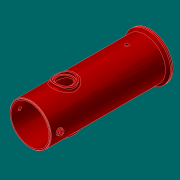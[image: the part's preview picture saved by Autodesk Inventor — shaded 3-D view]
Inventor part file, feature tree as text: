
AUTODESK INVENTOR PART (.ipt)
format: ipt  version: 2017.3 (Build 213256000, 256)  size: 425,472 bytes
history: native  units: in
note: dims shown in document units (in); Inventor stores cm internally (conversion verified against a paired STEP export)
features: extrude x11, sketch x8, fillet x4, chamfer x2, plane x2, pattern_circular x2, other x1
ambient origin geometry x8: Origin, YZ Plane, XZ Plane, XY Plane, X Axis, Y Axis, Z Axis, Center Point
bodies: Solid1 (feature_tree)
feature tree (30):
  extrude  "Extrusion1"  Depth=31.0in
  extrude  "Extrusion2"  Depth=34.75in
  extrude  "Extrusion3"  Depth=34.48in
  chamfer  "Chamfer1"  Distance=1.0in
  extrude  "Extrusion4"  Depth=0.125in TaperAngle=45.0deg
  chamfer  "Chamfer2"  Distance=0.5in
  fillet  "Fillet1"  Radius=0.0312in
  extrude  "Extrusion5"  Depth=17.3228in
  plane  "Work Plane1"
  sketch  "Sketch6"  dims[d16=0.0312in d17=0.125in d18=45.0deg d19=0.0312in]
  extrude  "Extrusion6"  Depth=0.0312in
  extrude  "Extrusion7"  Depth=0.0312in TaperAngle=0.0deg
  extrude  "Extrusion8"  Depth=0.0312in
  fillet  "Fillet2"  Radius=2.5in
  pattern_circular  "Circular Pattern1"  Count=212  [1 undecoded]
  plane  "Work Plane2"
  sketch  "Sketch7"  dims[d20=2.5984in d21=17.3228in]
  extrude  "Extrusion9"  Depth=0.0312in TaperAngle=0.0deg
  extrude  "Extrusion10"  Depth=0.0312in TaperAngle=0.0deg
  fillet  "Fillet3"  Radius=1.5in
  fillet  "Fillet4"  [1 undecoded]
  pattern_circular  "Circular Pattern2"  [2 undecoded]
  sketch  "Sketch1"  dims[d0=28.5in d1=31.0in]
  sketch  "Sketch2"  dims[d2=90.0in d3=0.0in d4=34.75in]
  sketch  "Sketch3"  dims[d5=2.0in d6=0.0in d7=34.48in d8=1.0in d9=0.0in]
  sketch  "Sketch4"  dims[d10=1.875in d11=0.125in d12=45.0deg]
  sketch  "Sketch5"  dims[d13=29.98in d14=0.5in d15=0.0in]
  sketch  "Sketch8"  dims[d22=10.5in d23=46.9291in d24=0.5in d25=0.0in d26=4.0in d27=2.5in d28=83.4646in d29=0.5in d30=0.0in d31=0.5in d32=0.0in d33=1.5in d34=0.0in d35=0.5in d36=0.7874in d37=360.0deg d39=15.0in d40=1.0in d41=0.0in d42=12.75in d43=34.75in d44=90.0in d45=0.0in d46=90.0in d47=0.0in d48=1.75in d49=0.0312in d50=0.7874in d51=360.0deg]
  other  "Srf1"
  extrude  "ExtrusionSrf1"  Depth=0.0312in TaperAngle=360.0deg
note: 4 required parameter values undecoded (feature->parameter linkage not recoverable at this tier; creation-order binding heuristic only, values carry confidence <= 0.55)
